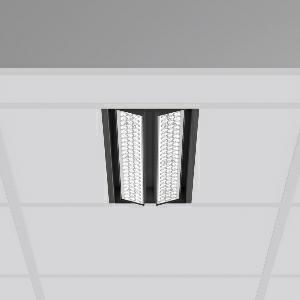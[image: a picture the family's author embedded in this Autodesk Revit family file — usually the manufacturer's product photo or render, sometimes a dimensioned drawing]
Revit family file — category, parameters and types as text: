
# Revit family: tx-move_901737_003_2_8e99
name_source: partatom
category: Lighting Fixtures
units: mm (PartAtom-declared; Revit-internal decimal feet)

## family parameters
Cut with Voids When Loaded = No
Host = Face
Light Source = No
Part Type = Normal
Room Calculation Point = No
Round Connector Dimension = Use Diameter
Shared = No

## types (1)
- MultiLumen 1 (1 x LED Modul 927, 2025 lm, 2700)
    Apparent Load = 32 VA
    Approval mark = CE
    CIE Flux Codes = 77 96 99 100 100
    Color Rendering = 92
    Color Temperature = 2700
    Default Elevation = 1800 mm
    Description = Series: TX-MOVE
Einlege/Einbau-Flächenstrahler. Housing: sheet steel, powder-coated. 2xSwivel range: 90°. High-efficiency LED units with optimum light control thanks to clear plastic (PC) lens optics. Spezielle Mikrostrukturen reduzieren Gelbsaum. Symmetrical light distribution. Best colour rendering with CRI >90 for fresh products and coloured textiles. Suitable for laying in grid ceiling module 625. Connected converter included in separate gearbox.Suitable for through-wiring.MultiLumen: Luminous flux adjustable in 3 steps. Accessories: Mounting frame for installation in suspended ceilings. Environmentally friendly and resource-saving due to replaceable and recyclable components. 
Colour: deep black, matt (RAL 9005)
Length: 622 mm
Width: 190 mm
Height: 39 mm
Cut-out length: 602 mm
Cut-out width: 174 mm
Recess height: 100 mm
Lamp: LED
Socket: without socket
Colour temperature: 2700K
Colour rendering index (CRI): 90
System power: 32 W
Rated luminous flux: 4050 lm
Luminous efficiency: 127 lm/W
System power 2: 43 W
Rated luminous flux 2: 5200 lm
Luminous efficiency 2: 121 lm/W
System power 3: 62 W
Rated luminous flux 3: 6850 lm
Luminous efficiency 3: 110 lm/W
Control gear: Regulated power supply
Protection class: I
Type of protection: IP 20
    Height = 0 mm  [stored 0 ft]
    Lamp = 1 x LED Modul 927
    Lamp Light Flux = 2025 lm
    Lamp count = 1
    Length = 622 mm
    Lifetime = 50000 h
    Luminous efficacy = 127 lm/W
    Manufacturer = RZB
    ModVariant = No
    Model = 901737.003.2
    Mounting Place = Ceiling, Wall
    Mounting Type = Recessed
    Number of Poles = 1
    OnlyDefault = Yes
    Power Factor = 1
    Product Name = TX-MOVE
    Product group = Recessed projectors
    ProductGroupID = 401
    Protection Class = Protection class I
    Protection Degree = IP 20
    RLX_Detail_Level = 1
    RLX_Emergency_Light_Flux = 0 lm
    RLX_Emergency_Type = 0
    RLX_Emergency_Type_DB = No
    RlxData = <blob elided: 35741 chars, md5=892ab3f1>
    Socket = socket
    Standby Power = 0 W
    System Light Flux = 4050 lm
    System Power = 32 W
    Type Comments = MultiLumen 1
    Type Image = 901737.003.jpg
    URL = http://relux.com
    VarID = multilumen_1
    Voltage = 230 V
    Voltage Range = 220-240 V
    Weight = 0.00 kg
    Width = 190 mm  [stored 0.62336 ft]

note: [stored X ft] marks values corroborated as IEEE doubles in the binary element streams (Revit-internal decimal feet)

## geometry (parser evidence)
native form markers: Blend x4, Sweep x15
no freeform markers — native parametric forms only
